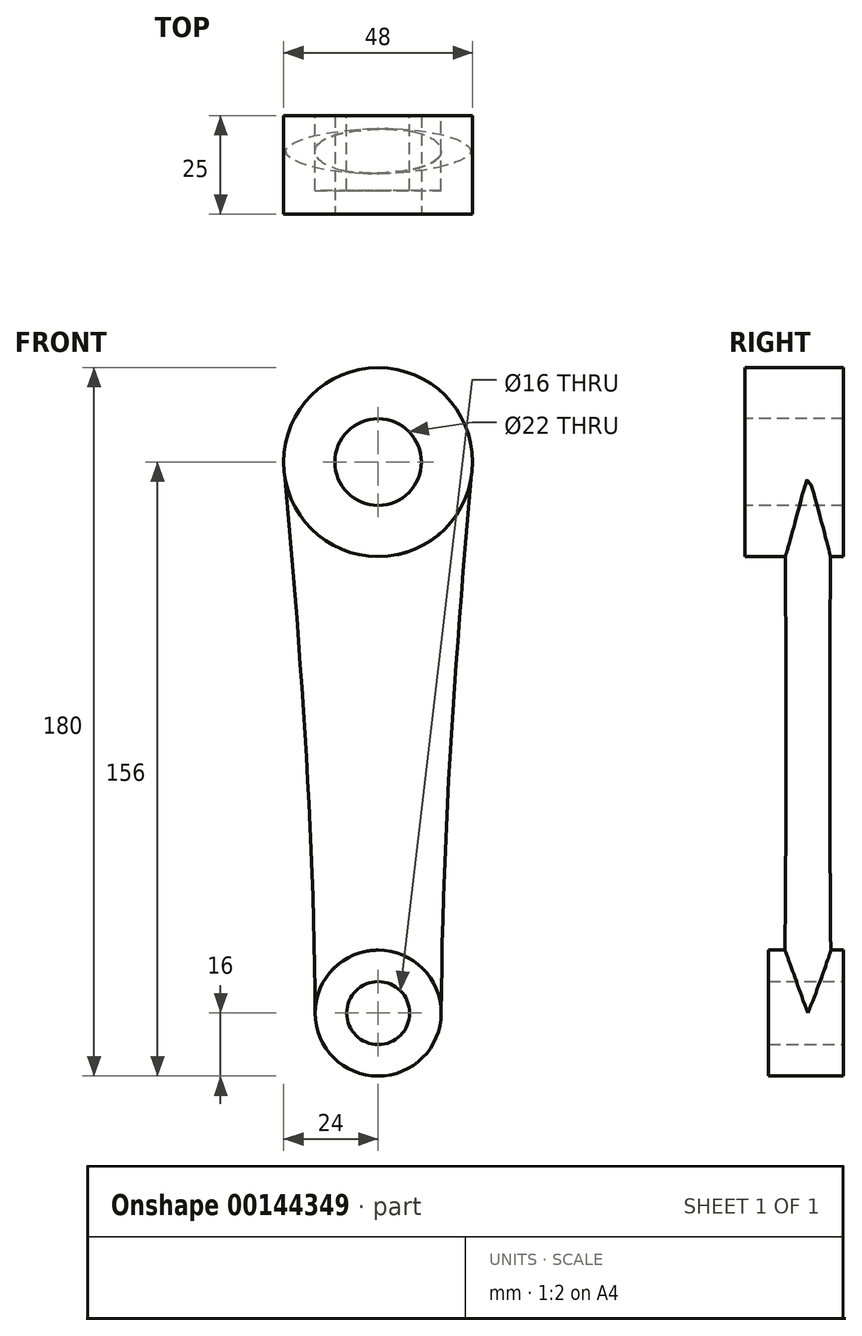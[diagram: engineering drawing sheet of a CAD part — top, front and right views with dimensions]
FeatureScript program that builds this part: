
annotation { "Feature Type Name" : "Feature", "Feature Type Description" : "" }
export const myFeature = defineFeature(function(context is Context, id is Id, definition is map)
    precondition{}
    {
        {
            var Q0;
            Q0=qCreatedBy(makeId("Front.planeOp"),FACE);
            var sketch = newSketch(context, id + "F0", { "sketchPlane" : qUnion([Q0])});
            skCircle(sketch, "E0", {"center": v(0, 0) * mm, "radius": 8 * mm});
            skCircle(sketch, "E1", {"center": v(0, 0) * mm, "radius": 16 * mm});
            skSolve(sketch);
        }
        {
            var Q0;
            Q0=qSketchRegion(id+"F0",true);
            extrude(context, id + "F1", {"entities" : qUnion([Q0]), "endBound" : BoundingType.SYMMETRIC, "depth" : 19 * mm});
        }
        {
            var Q0;
            Q0=qCreatedBy(makeId("Front.planeOp"),FACE);
            var sketch = newSketch(context, id + "F2", { "sketchPlane" : qUnion([Q0])});
            skCircle(sketch, "E2", {"center": v(0, 140) * mm, "radius": 11 * mm});
            skCircle(sketch, "E3", {"center": v(0, 140) * mm, "radius": 24 * mm});
            skSolve(sketch);
        }
        {
            var Q0;
            Q0=qSketchRegion(id+"F2",true);
            extrude(context, id + "F3", {"entities" : qUnion([Q0]), "oppositeDirection" : true, "depth" : 9.5 * mm});
        }
        {
            var Q0;
            Q0=makeQuery(id+"F3.opExtrude","CAP_FACE",FACE,{"disambiguationData":[OSD([sQuery(id+"F2.wireOp",EDGE,"E2"),sQuery(id+"F2.wireOp",EDGE,"E3")])],"isStart":true});
            var sketch = newSketch(context, id + "F4", { "sketchPlane" : qUnion([Q0])});
            skCircle(sketch, "E4.0", {"center": v(0, 140) * mm, "radius": 24 * mm});
            skCircle(sketch, "E5.0", {"center": v(0, 140) * mm, "radius": 11 * mm});
            skSolve(sketch);
        }
        {
            var Q0;
            Q0=qSketchRegion(id+"F4",true);
            extrude(context, id + "F5", {"entities" : qUnion([Q0]), "operationType" : NewBodyOperationType.ADD, "depth" : (25 - 9.5) * mm});
        }
        {
            var Q0;
            Q0=qCreatedBy(makeId("Top.planeOp"),FACE);
            var sketch = newSketch(context, id + "F6", { "sketchPlane" : qUnion([Q0])});
            skEllipse(sketch, "E6", {"center": v(0, 0.5) * mm, "majorRadius": 16 * mm, "minorRadius": 6 * mm, "majorAxis": v(1, 0)});
            skPoint(sketch, "E7", {"position": v(0, 6.5) * mm});
            skLineSegment(sketch, "E8", {"start": v(16, 9.5) * mm, "end": v(16, -9.5) * mm, "construction": true});
            skSolve(sketch);
        }
        {
            var Q0;
            Q0=sQuery(id+"F2.wireOp",VERTEX,"E2.center");
            var Q1;
            Q1=qCreatedBy(makeId("Top.planeOp"),FACE);
            cPlane(context, id + "F7", {"entities" : qUnion([Q0, Q1]), "cplaneType" : CPlaneType.PLANE_POINT, "offset" : 25 * mm, "width" : 150 * mm, "height" : 150 * mm});
        }
        {
            var Q0;
            Q0=qCreatedBy(id+"F7.planeOp",FACE);
            var sketch = newSketch(context, id + "F8", { "sketchPlane" : qUnion([Q0])});
            skEllipse(sketch, "E9", {"center": v(0, 0.5) * mm, "majorRadius": 24 * mm, "minorRadius": 6 * mm, "majorAxis": v(1, 0)});
            skPoint(sketch, "E10", {"position": v(0, 6.5) * mm});
            skLineSegment(sketch, "E11", {"start": v(24, 9.5) * mm, "end": v(24, -15.5) * mm, "construction": true});
            skSolve(sketch);
        }
        {
            var Q0;
            Q0=makeQuery(id+"F6.imprint","IMPRINT",FACE,{"disambiguationData":[TD([[makeQuery(id+"F6.imprint","IMPRINT",EDGE,{"derivedFrom":sQuery(id+"F6.wireOp",EDGE,"E6")}),1.0]])]});
            var Q1;
            Q1=makeQuery(id+"F8.imprint","IMPRINT",FACE,{"disambiguationData":[TD([[makeQuery(id+"F8.imprint","IMPRINT",EDGE,{"derivedFrom":sQuery(id+"F8.wireOp",EDGE,"E9")}),1.0]])]});
            loft(context, id + "F9", {"operationType" : NewBodyOperationType.ADD, "sheetProfilesArray" : [{ "sheetProfileEntities" : qUnion([Q0]) }, { "sheetProfileEntities" : qUnion([Q1]) }]});
        }
        {
            var Q0;
            Q0=makeQuery(id+"F1.opExtrude","CAP_FACE",FACE,{"disambiguationData":[OSD([sQuery(id+"F0.wireOp",EDGE,"E0"),sQuery(id+"F0.wireOp",EDGE,"E1")])],"isStart":false});
            var sketch = newSketch(context, id + "F10", { "sketchPlane" : qUnion([Q0])});
            skCircle(sketch, "E12.0", {"center": v(0, 0) * mm, "radius": 8 * mm});
            skSolve(sketch);
        }
        {
            var Q0;
            Q0=qSketchRegion(id+"F10",true);
            extrude(context, id + "F11", {"entities" : qUnion([Q0]), "operationType" : NewBodyOperationType.REMOVE, "endBound" : BoundingType.THROUGH_ALL, "oppositeDirection" : true, "depth" : 25 * mm});
        }
        {
            var Q0;
            Q0=makeQuery(id+"F5.opExtrude","CAP_FACE",FACE,{"disambiguationData":[OSD([sQuery(id+"F4.wireOp",EDGE,"E4.0"),sQuery(id+"F4.wireOp",EDGE,"E5.0")])],"isStart":false});
            var sketch = newSketch(context, id + "F12", { "sketchPlane" : qUnion([Q0])});
            skCircle(sketch, "E13.0", {"center": v(0, 140) * mm, "radius": 11 * mm});
            skSolve(sketch);
        }
        {
            var Q0;
            Q0=qSketchRegion(id+"F12",true);
            extrude(context, id + "F13", {"entities" : qUnion([Q0]), "operationType" : NewBodyOperationType.REMOVE, "endBound" : BoundingType.THROUGH_ALL, "oppositeDirection" : true, "depth" : 25 * mm});
        }
    });
